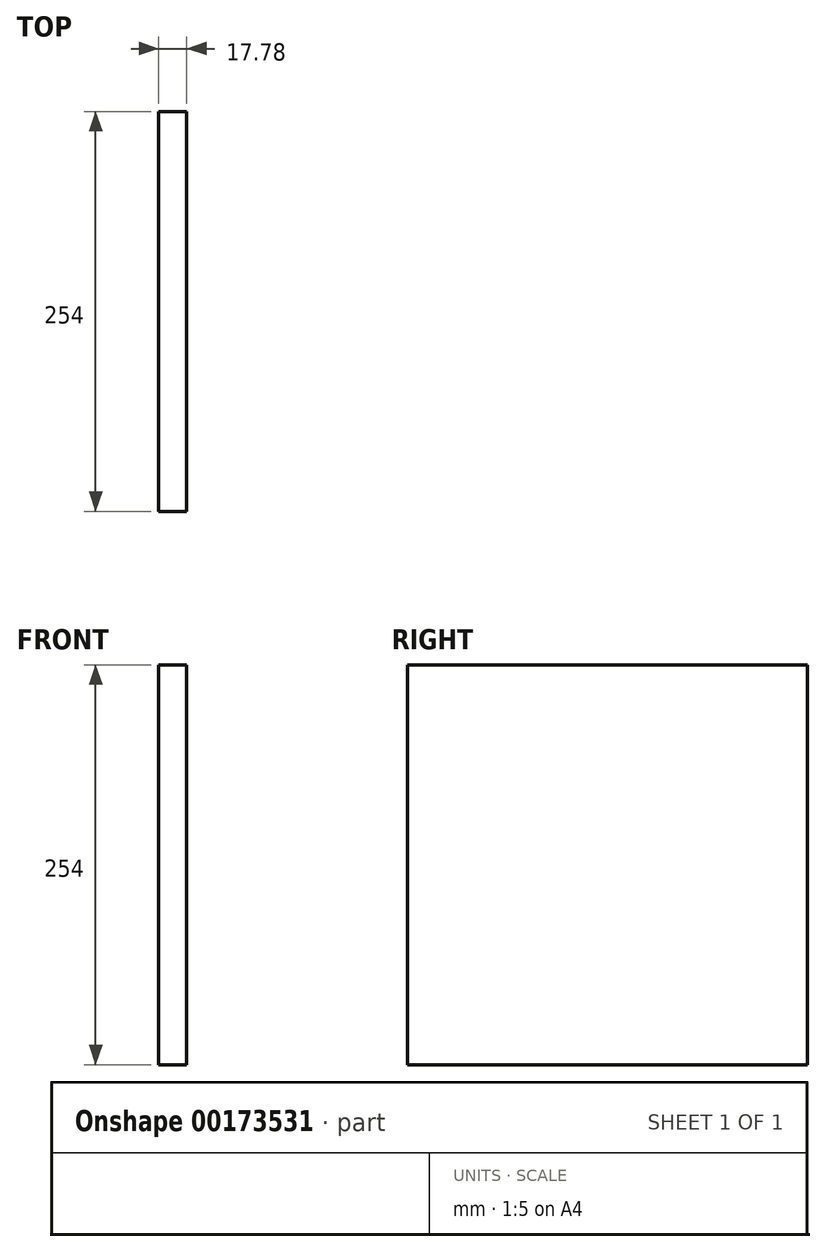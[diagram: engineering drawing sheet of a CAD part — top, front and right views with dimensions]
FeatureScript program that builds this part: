
annotation { "Feature Type Name" : "Feature", "Feature Type Description" : "" }
export const myFeature = defineFeature(function(context is Context, id is Id, definition is map)
    precondition{}
    {
        {
            var Q0;
            Q0=qCreatedBy(makeId("Right.planeOp"),FACE);
            var sketch = newSketch(context, id + "F0", { "sketchPlane" : qUnion([Q0])});
            skLineSegment(sketch, "E0.bottom", {"start": v(-133.13, 122.29) * mm, "end": v(120.87, 122.29) * mm});
            skLineSegment(sketch, "E0.top", {"start": v(-133.13, -131.71) * mm, "end": v(120.87, -131.71) * mm});
            skLineSegment(sketch, "E0.left", {"start": v(-133.13, 122.29) * mm, "end": v(-133.13, -131.71) * mm});
            skLineSegment(sketch, "E0.right", {"start": v(120.87, 122.29) * mm, "end": v(120.87, -131.71) * mm});
            skSolve(sketch);
        }
        {
            var Q0;
            Q0=makeQuery(id+"F0.imprint","IMPRINT",FACE,{"disambiguationData":[TD([[makeQuery(id+"F0.imprint","IMPRINT",EDGE,{"derivedFrom":sQuery(id+"F0.wireOp",EDGE,"E0.bottom")}),-1.0]])]});
            extrude(context, id + "F1", {"entities" : qUnion([Q0]), "depth" : 17.78 * mm});
        }
    });
